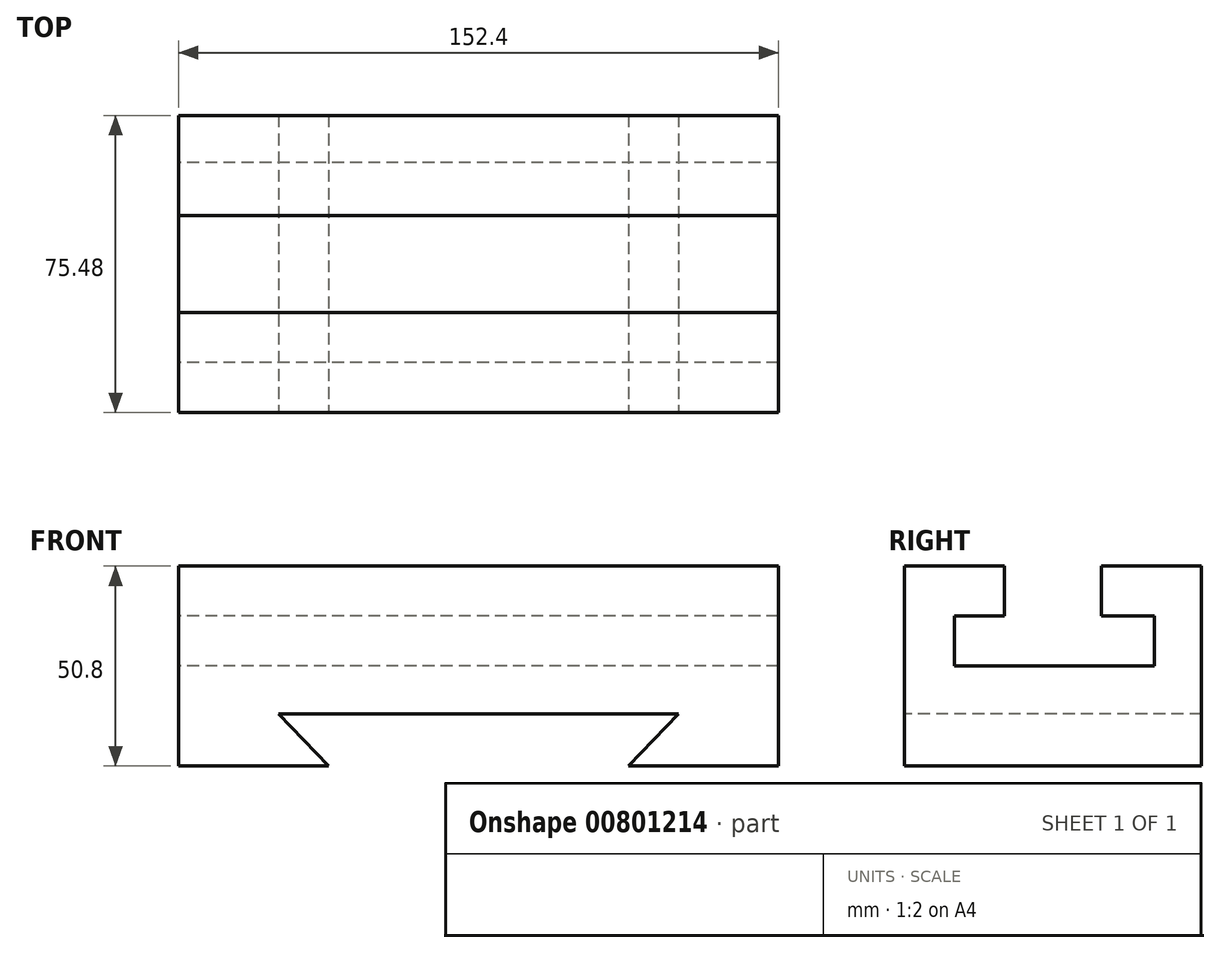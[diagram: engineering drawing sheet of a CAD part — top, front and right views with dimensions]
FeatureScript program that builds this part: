
annotation { "Feature Type Name" : "Feature", "Feature Type Description" : "" }
export const myFeature = defineFeature(function(context is Context, id is Id, definition is map)
    precondition{}
    {
        {
            var Q0;
            Q0=qCreatedBy(makeId("Right.planeOp"),FACE);
            var sketch = newSketch(context, id + "F0", { "sketchPlane" : qUnion([Q0])});
            skLineSegment(sketch, "E0", {"start": v(-84.81, -50.8) * mm, "end": v(71.3, -50.8) * mm});
            skLineSegment(sketch, "E1", {"start": v(71.3, -50.8) * mm, "end": v(71.3, 0) * mm});
            skLineSegment(sketch, "E2", {"start": v(71.3, 0) * mm, "end": v(45.9, 0) * mm});
            skLineSegment(sketch, "E3", {"start": v(45.9, 0) * mm, "end": v(45.9, -12.7) * mm});
            skLineSegment(sketch, "E4", {"start": v(45.9, -12.7) * mm, "end": v(59.33, -12.7) * mm});
            skLineSegment(sketch, "E5", {"start": v(59.33, -12.7) * mm, "end": v(59.33, -25.4) * mm});
            skLineSegment(sketch, "E6", {"start": v(59.33, -25.4) * mm, "end": v(8.53, -25.4) * mm});
            skLineSegment(sketch, "E7", {"start": v(8.53, -25.4) * mm, "end": v(8.53, -12.7) * mm});
            skLineSegment(sketch, "E8", {"start": v(8.53, -12.7) * mm, "end": v(21.23, -12.7) * mm});
            skLineSegment(sketch, "E9", {"start": v(21.23, -12.7) * mm, "end": v(21.23, 0) * mm});
            skLineSegment(sketch, "E10", {"start": v(21.23, 0) * mm, "end": v(-4.17, 0) * mm});
            skLineSegment(sketch, "E11", {"start": v(-4.17, 0) * mm, "end": v(-4.17, -50.8) * mm});
            skSolve(sketch);
        }
        {
            var Q0;
            {var subQ0=sQuery(id+"F0.wireOp",EDGE,"E1");Q0=makeQuery(id+"F0.imprint","IMPRINT",FACE,{"disambiguationData":[TD([[makeQuery(id+"F0.imprint","IMPRINT",EDGE,{"derivedFrom":subQ0}),1.0]])]});}
            extrude(context, id + "F1", {"entities" : qUnion([Q0]), "depth" : 152.4 * mm, "offsetDistance" : 25.4 * mm});
        }
        {
            var Q0;
            Q0=makeQuery(id+"F1.opExtrude","SWEPT_FACE",FACE,{"disambiguationData":[OSD([sQuery(id+"F0.wireOp",EDGE,"E11")])]});
            var sketch = newSketch(context, id + "F2", { "sketchPlane" : qUnion([Q0])});
            skLineSegment(sketch, "E12", {"start": v(38.1, -50.8) * mm, "end": v(25.4, -37.56) * mm});
            skLineSegment(sketch, "E13", {"start": v(25.4, -37.56) * mm, "end": v(127, -37.56) * mm});
            skLineSegment(sketch, "E14", {"start": v(127, -37.56) * mm, "end": v(114.3, -50.8) * mm});
            skSolve(sketch);
        }
        {
            var Q0;
            Q0 = qSketchRegion(id + "F2", true);
            var Q1;
            {var subQ0=sQuery(id+"F2.wireOp",EDGE,"E12");Q1=makeQuery(id+"F2.imprint","IMPRINT",FACE,{"disambiguationData":[TD([[makeQuery(id+"F2.imprint","IMPRINT",EDGE,{"derivedFrom":subQ0}),-1.0]])]});}
            extrude(context, id + "F3", {"entities" : qUnion([Q0, Q1]), "operationType" : NewBodyOperationType.REMOVE, "endBound" : BoundingType.THROUGH_ALL, "oppositeDirection" : true, "depth" : 25.4 * mm, "offsetDistance" : 25.4 * mm});
        }
    });
